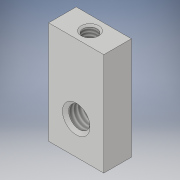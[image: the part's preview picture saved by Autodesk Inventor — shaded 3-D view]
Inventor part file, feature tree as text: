
AUTODESK INVENTOR PART (.ipt)
format: ipt  version: 2019.4 (Build 234330000, 330)  size: 122,368 bytes
history: native  units: in
note: dims shown in document units (in); Inventor stores cm internally (conversion verified against a paired STEP export)
features: sketch x3, hole x2, extrude x1, chamfer x1
ambient origin geometry x8: Origin, YZ Plane, XZ Plane, XY Plane, X Axis, Y Axis, Z Axis, Center Point
bodies: Solid1 (feature_tree)
feature tree (7):
  extrude  "Extrusion1"  Depth=0.93in
  hole  "6 MM Hole"  [1 undecoded]
  hole  "Hole2"  [1 undecoded]
  chamfer  "Chamfer1"  Distance=0.25in
  sketch  "Sketch1"  dims[d0=0.5in d1=0.93in]
  sketch  "Sketch2"  dims[d2=0.25in d3=0.0in d4=0.25in]
  sketch  "Sketch3"  dims[d5=0.3in d6=0.194in d7=0.472in d8=0.25in d9=0.25in d10=90.0deg d11=0.673in d12=0.8108in d13=0.125in d14=0.25in d15=0.128in d16=0.4in d17=0.16in d18=0.25in d19=90.0deg d20=0.475in d21=0.8108in d22=0.02in d23=0.125in d24=45.0deg]
note: 2 required parameter values undecoded (feature->parameter linkage not recoverable at this tier; creation-order binding heuristic only, values carry confidence <= 0.55)
